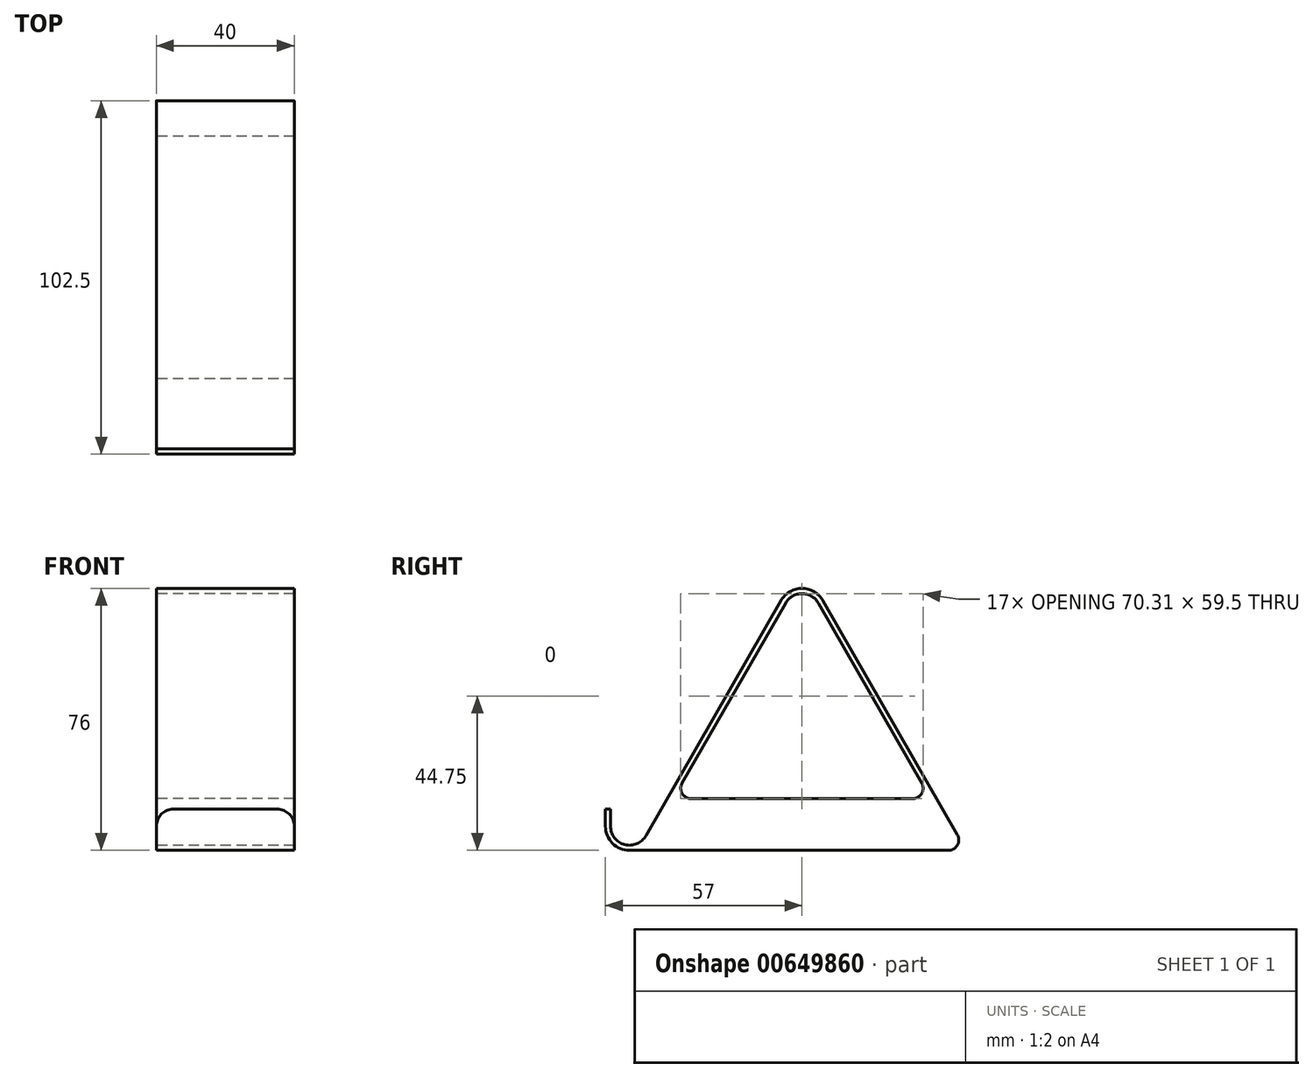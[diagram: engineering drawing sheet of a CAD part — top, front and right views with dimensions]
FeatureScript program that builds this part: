
annotation { "Feature Type Name" : "Feature", "Feature Type Description" : "" }
export const myFeature = defineFeature(function(context is Context, id is Id, definition is map)
    precondition{}
    {
        {
            var Q0;
            Q0=qCreatedBy(makeId("Right.planeOp"),FACE);
            var sketch = newSketch(context, id + "F0", { "sketchPlane" : qUnion([Q0])});
            skArc(sketch, "E0", {"start": v(-7, 0) * mm, "mid": v(-4.95, -4.95) * mm, "end": v(0, -7) * mm});
            skArc(sketch, "E1", {"start": v(54.77, 64.74) * mm, "mid": v(50, 67.5) * mm, "end": v(45.23, 64.74) * mm});
            skLineSegment(sketch, "E2", {"start": v(15.24, 12.5) * mm, "end": v(45.23, 64.74) * mm});
            skLineSegment(sketch, "E3", {"start": v(50, 62) * mm, "end": v(50, -58.47) * mm, "construction": true});
            skLineSegment(sketch, "E4", {"start": v(0, -7) * mm, "end": v(92.5, -7) * mm, "construction": true});
            skPoint(sketch, "E5.orphan", {"position": v(93.93, -3.48) * mm});
            skLineSegment(sketch, "E6", {"start": v(-7, 0) * mm, "end": v(-7, 5) * mm});
            skLineSegment(sketch, "E7.0", {"start": v(-5.5, 0) * mm, "end": v(-5.5, 5) * mm});
            skLineSegment(sketch, "E7.1", {"start": v(95.1, -2.5) * mm, "end": v(56.07, 65.48) * mm});
            skArc(sketch, "E7.2", {"start": v(56.07, 65.48) * mm, "mid": v(50, 69) * mm, "end": v(43.93, 65.48) * mm});
            skLineSegment(sketch, "E7.3", {"start": v(4.77, -2.74) * mm, "end": v(43.93, 65.48) * mm});
            skArc(sketch, "E7.4", {"start": v(-5.5, 0) * mm, "mid": v(-1.42, -5.31) * mm, "end": v(4.77, -2.74) * mm});
            skLineSegment(sketch, "E8", {"start": v(-7, 5) * mm, "end": v(-5.5, 5) * mm});
            skLineSegment(sketch, "E9", {"start": v(0, -7) * mm, "end": v(97.68, -7) * mm});
            skLineSegment(sketch, "E10.0", {"start": v(17.84, 8) * mm, "end": v(82.16, 8) * mm});
            skPoint(sketch, "E11.orphan", {"position": v(6.07, -3.48) * mm});
            skLineSegment(sketch, "E12.trimOffspring", {"start": v(84.76, 12.5) * mm, "end": v(54.77, 64.74) * mm});
            skPoint(sketch, "E13.visualSharp", {"position": v(12.66, 8) * mm});
            skArc(sketch, "E13.filletArc", {"start": v(15.24, 12.5) * mm, "mid": v(15.25, 9.5) * mm, "end": v(17.84, 8) * mm});
            skArc(sketch, "E14.filletArc", {"start": v(92.5, -7) * mm, "mid": v(95.1, -5.5) * mm, "end": v(95.1, -2.5) * mm});
            skPoint(sketch, "E15.visualSharp", {"position": v(87.34, 8) * mm});
            skArc(sketch, "E15.filletArc", {"start": v(82.16, 8) * mm, "mid": v(84.75, 9.5) * mm, "end": v(84.76, 12.5) * mm});
            skSolve(sketch);
        }
        {
            var Q0;
            {var subQ0=sQuery(id+"F0.wireOp",EDGE,"E0");Q0=makeQuery(id+"F0.imprint","IMPRINT",FACE,{"disambiguationData":[TD([[makeQuery(id+"F0.imprint","IMPRINT",EDGE,{"derivedFrom":subQ0}),1.0]])]});}
            extrude(context, id + "F1", {"entities" : qUnion([Q0]), "depth" : 40 * mm, "offsetDistance" : 25 * mm});
        }
        {
            var Q0;
            Q0=makeQuery(id+"F1.opExtrude","CAP_EDGE",EDGE,{"disambiguationData":[OSD([sQuery(id+"F0.wireOp",EDGE,"E8")])],"isStart":false});
            var Q1;
            Q1=makeQuery(id+"F1.opExtrude","CAP_EDGE",EDGE,{"disambiguationData":[OSD([sQuery(id+"F0.wireOp",EDGE,"E8")])],"isStart":true});
            fillet(context, id + "F2", {"entities" : qUnion([Q0, Q1]), "radius" : 5 * mm, "tangentPropagation" : true, "allowEdgeOverflow" : false});
        }
    });
